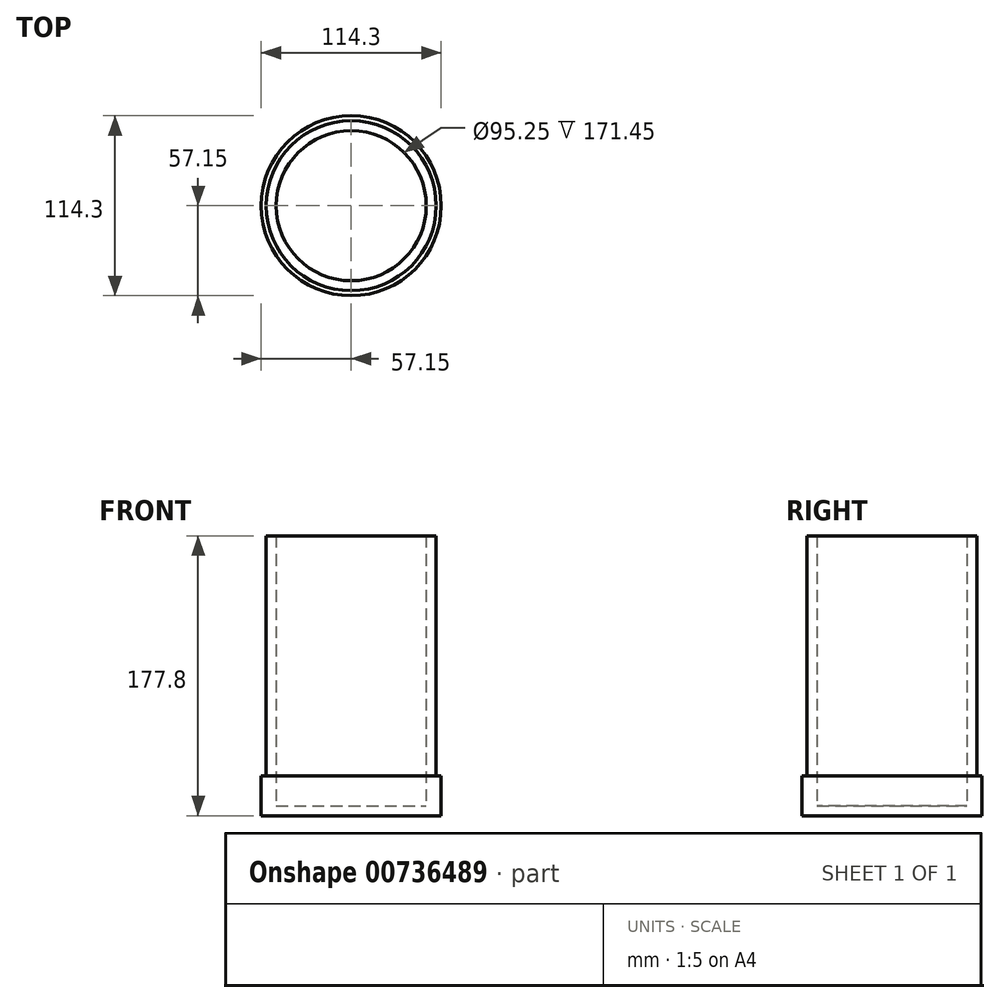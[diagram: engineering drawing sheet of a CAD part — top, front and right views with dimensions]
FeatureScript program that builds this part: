
annotation { "Feature Type Name" : "Feature", "Feature Type Description" : "" }
export const myFeature = defineFeature(function(context is Context, id is Id, definition is map)
    precondition{}
    {
        {
            var Q0;
            Q0=qCreatedBy(makeId("Front.planeOp"),FACE);
            var sketch = newSketch(context, id + "F0", { "sketchPlane" : qUnion([Q0])});
            skLineSegment(sketch, "E0.bottom", {"start": v(0, 0) * mm, "end": v(-57.15, 0) * mm});
            skLineSegment(sketch, "E0.top", {"start": v(0, 6.35) * mm, "end": v(-57.15, 6.35) * mm});
            skLineSegment(sketch, "E0.left", {"start": v(0, 0) * mm, "end": v(0, 6.35) * mm});
            skLineSegment(sketch, "E0.right", {"start": v(-57.15, 0) * mm, "end": v(-57.15, 6.35) * mm});
            skLineSegment(sketch, "E1.bottom", {"start": v(-57.15, 6.35) * mm, "end": v(-53.98, 6.35) * mm});
            skLineSegment(sketch, "E1.top", {"start": v(-57.15, 25.4) * mm, "end": v(-53.98, 25.4) * mm});
            skLineSegment(sketch, "E1.left", {"start": v(-57.15, 6.35) * mm, "end": v(-57.15, 25.4) * mm});
            skLineSegment(sketch, "E1.right", {"start": v(-53.98, 6.35) * mm, "end": v(-53.98, 25.4) * mm});
            skLineSegment(sketch, "E2.bottom", {"start": v(-53.98, 6.35) * mm, "end": v(-47.63, 6.35) * mm});
            skLineSegment(sketch, "E2.top", {"start": v(-53.98, 177.8) * mm, "end": v(-47.63, 177.8) * mm});
            skLineSegment(sketch, "E2.left", {"start": v(-53.98, 6.35) * mm, "end": v(-53.98, 177.8) * mm});
            skLineSegment(sketch, "E2.right", {"start": v(-47.63, 6.35) * mm, "end": v(-47.63, 177.8) * mm});
            skSolve(sketch);
        }
        {
            var Q0;
            Q0 = qSketchRegion(id + "F0", true);
            var Q1;
            Q1=sQuery(id+"F0.wireOp",EDGE,"E0.left");
            revolve(context, id + "F1", {"surfaceOperationType" : NewSurfaceOperationType.NEW, "entities" : qUnion([Q0]), "axis" : qUnion([Q1]), "revolveType" : RevolveType.FULL});
        }
        {
            var Q0;
            Q0=qCreatedBy(makeId("Front.planeOp"),FACE);
            cPlane(context, id + "F2", {"entities" : qUnion([Q0]), "cplaneType" : CPlaneType.OFFSET, "offset" : 177.8 * mm, "width" : 152.4 * mm, "height" : 152.4 * mm});
        }
    });
